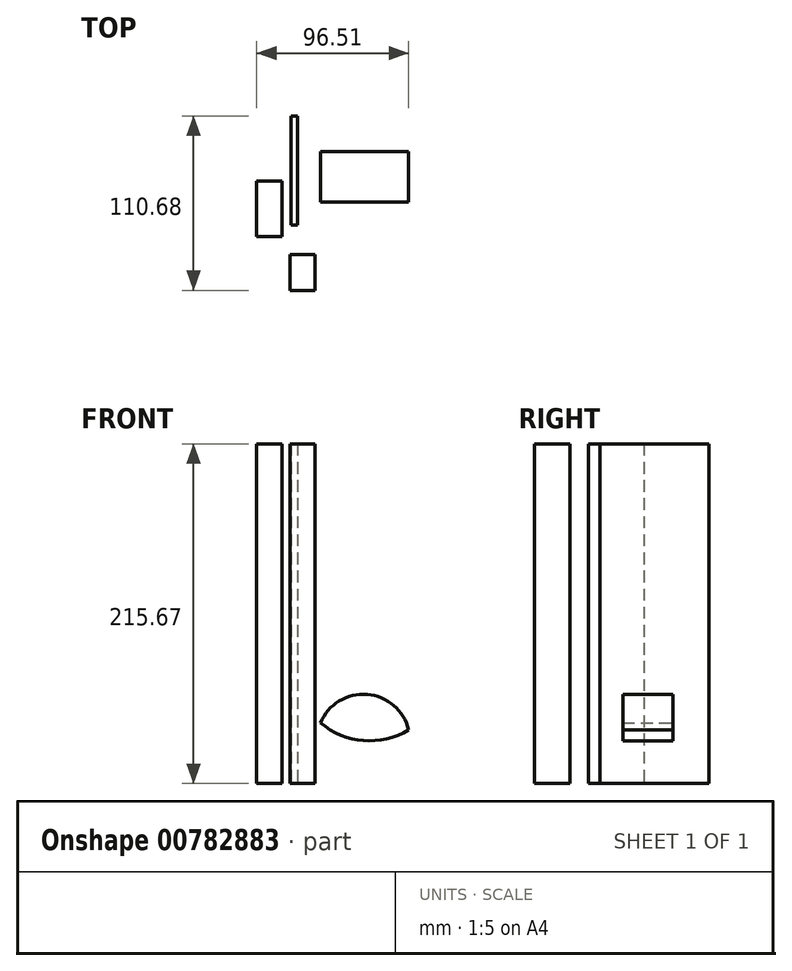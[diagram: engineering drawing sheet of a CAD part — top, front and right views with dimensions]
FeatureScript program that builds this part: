
annotation { "Feature Type Name" : "Feature", "Feature Type Description" : "" }
export const myFeature = defineFeature(function(context is Context, id is Id, definition is map)
    precondition{}
    {
        {
            var Q0;
            Q0=qCreatedBy(makeId("Front.planeOp"),FACE);
            var sketch = newSketch(context, id + "F0", { "sketchPlane" : qUnion([Q0])});
            skCircle(sketch, "E0", {"center": v(20.68, 75.05) * mm, "radius": 48.03 * mm});
            skCircle(sketch, "E1", {"center": v(16.77, 27.18) * mm, "radius": 29.48 * mm});
            skSolve(sketch);
        }
        {
            var Q0;
            {var subQ0=sQuery(id+"F0.wireOp",EDGE,"E1");var subQ1=sQuery(id+"F0.wireOp",EDGE,"E0");var subQ2=makeQuery(id+"F0.imprint","INTERSECT",VERTEX,{"disambiguationData":[OD(0.0)],"derivedFrom":[subQ1,subQ0]});Q0=makeQuery(id+"F0.imprint","IMPRINT",FACE,{"disambiguationData":[TD([[makeQuery(id+"F0.imprint","IMPRINT",EDGE,{"disambiguationData":[TD([[subQ2,-1.0]])],"derivedFrom":subQ1}),1.0]])]});}
            extrude(context, id + "F1", {"entities" : qUnion([Q0]), "depth" : 31.95 * mm, "offsetDistance" : 25.4 * mm});
        }
        {
            var Q0;
            Q0=qCreatedBy(makeId("Top.planeOp"),FACE);
            var sketch = newSketch(context, id + "F2", { "sketchPlane" : qUnion([Q0])});
            skLineSegment(sketch, "E2.bottom", {"start": v(-34.81, -18.5) * mm, "end": v(-51.04, -18.5) * mm});
            skLineSegment(sketch, "E2.top", {"start": v(-34.81, -53.79) * mm, "end": v(-51.04, -53.79) * mm});
            skLineSegment(sketch, "E2.left", {"start": v(-34.81, -18.5) * mm, "end": v(-34.81, -53.79) * mm});
            skLineSegment(sketch, "E2.right", {"start": v(-51.04, -18.5) * mm, "end": v(-51.04, -53.79) * mm});
            skPoint(sketch, "E3.firstSnap0", {"position": v(-34.81, -36.15) * mm});
            skPoint(sketch, "E3.oppositeSnap0", {"position": v(-34.81, -36.15) * mm});
            skLineSegment(sketch, "E3.bottom", {"start": v(-18.32, -36.15) * mm, "end": v(-15.45, -36.15) * mm});
            skLineSegment(sketch, "E3.top", {"start": v(-18.32, -36.15) * mm, "end": v(-15.45, -36.15) * mm});
            skLineSegment(sketch, "E3.left", {"start": v(-18.32, -36.15) * mm, "end": v(-18.32, -36.15) * mm});
            skLineSegment(sketch, "E3.right", {"start": v(-15.45, -36.15) * mm, "end": v(-15.45, -36.15) * mm});
            skLineSegment(sketch, "E4.bottom", {"start": v(-26.75, 9.71) * mm, "end": v(-25.16, 9.71) * mm});
            skLineSegment(sketch, "E4.top", {"start": v(-26.75, 10.27) * mm, "end": v(-25.16, 10.27) * mm});
            skLineSegment(sketch, "E4.left", {"start": v(-26.75, 9.71) * mm, "end": v(-26.75, 10.27) * mm});
            skLineSegment(sketch, "E4.right", {"start": v(-25.16, 9.71) * mm, "end": v(-25.16, 10.27) * mm});
            skLineSegment(sketch, "E5.bottom", {"start": v(-29.27, -46.5) * mm, "end": v(-25.16, -46.5) * mm});
            skLineSegment(sketch, "E5.top", {"start": v(-29.27, 22.65) * mm, "end": v(-25.16, 22.65) * mm});
            skLineSegment(sketch, "E5.left", {"start": v(-29.27, -46.5) * mm, "end": v(-29.27, 22.65) * mm});
            skLineSegment(sketch, "E5.right", {"start": v(-25.16, -46.5) * mm, "end": v(-25.16, 22.65) * mm});
            skLineSegment(sketch, "E6.bottom", {"start": v(-13.83, -88.03) * mm, "end": v(-29.8, -88.03) * mm});
            skLineSegment(sketch, "E6.top", {"start": v(-13.83, -65.4) * mm, "end": v(-29.8, -65.4) * mm});
            skLineSegment(sketch, "E6.left", {"start": v(-13.83, -88.03) * mm, "end": v(-13.83, -65.4) * mm});
            skLineSegment(sketch, "E6.right", {"start": v(-29.8, -88.03) * mm, "end": v(-29.8, -65.4) * mm});
            skSolve(sketch);
        }
        {
            var Q0;
            Q0 = qSketchRegion(id + "F2", true);
            var Q1;
            Q1=makeQuery(id+"F2.imprint","IMPRINT",FACE,{"disambiguationData":[TD([[makeQuery(id+"F2.imprint","IMPRINT",EDGE,{"derivedFrom":sQuery(id+"F2.wireOp",EDGE,"E2.bottom")}),1.0]])]});
            extrude(context, id + "F3", {"entities" : qUnion([Q0, Q1]), "depth" : 215.67 * mm, "offsetDistance" : 25.4 * mm});
        }
    });
